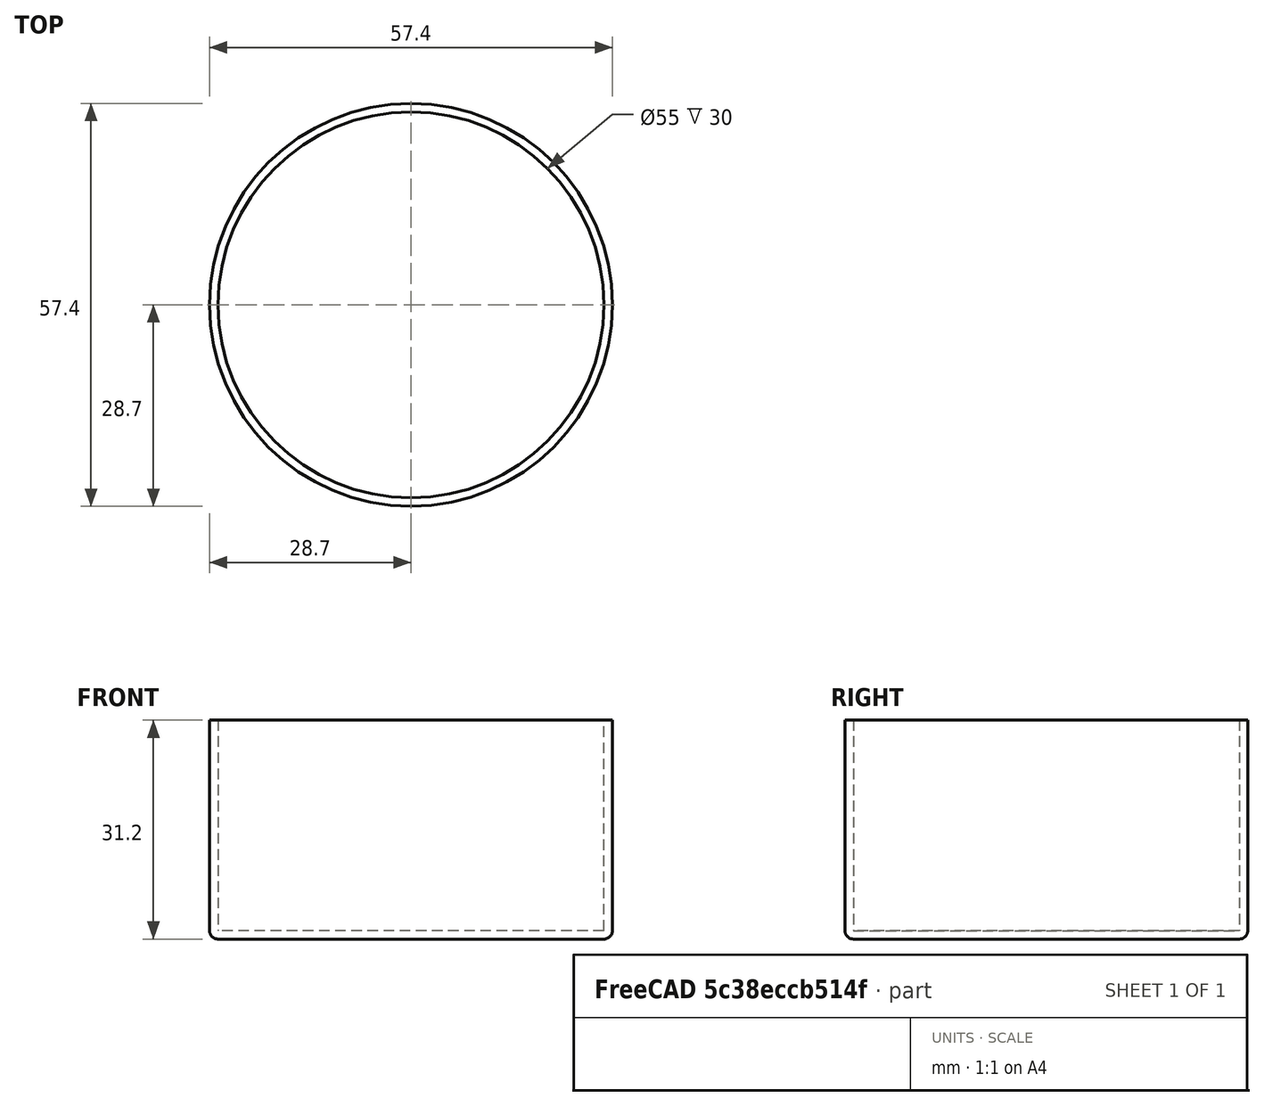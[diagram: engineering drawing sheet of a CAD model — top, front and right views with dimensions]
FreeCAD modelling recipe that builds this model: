
FCSTD DOCUMENT  (FreeCAD 1.0R39319 (Git))
Label: pepperShakeCover
License: All rights reserved
LicenseURL: https://en.wikipedia.org/wiki/All_rights_reserved
objects: PartDesign::AdditiveCylinder×1, PartDesign::Thickness×1, PartDesign::Body×1
note: 7 computed .brp shape members not serialized (recipe doc carries the construction recipe); baked Part::Feature solids carry a one-line shape summary decoded from their .brp

FEATURE [PartDesign::AdditiveCylinder] Cylinder
  Angle = 360
  AttacherType = Attacher::AttachEngine3D
  FirstAngle = 0
  Height = 30
  Radius = 27.5
  Refine = true
  SecondAngle = 0
  Suppressed = false
  expr: Radius = 55 mm / 2
FEATURE [PartDesign::Thickness] Thickness
  Base = -> Cylinder [Face3]
  BaseFeature = -> Cylinder
  Intersection = false
  Join = 0
  Mode = 0
  Refine = true
  SupportTransform = false
  Suppressed = false
  Value = 1.2
FEATURE [PartDesign::Body] Body
  AllowCompound = false
  Group = -> [Cylinder,Thickness]
  Origin = -> Origin
  Tip = -> Thickness
